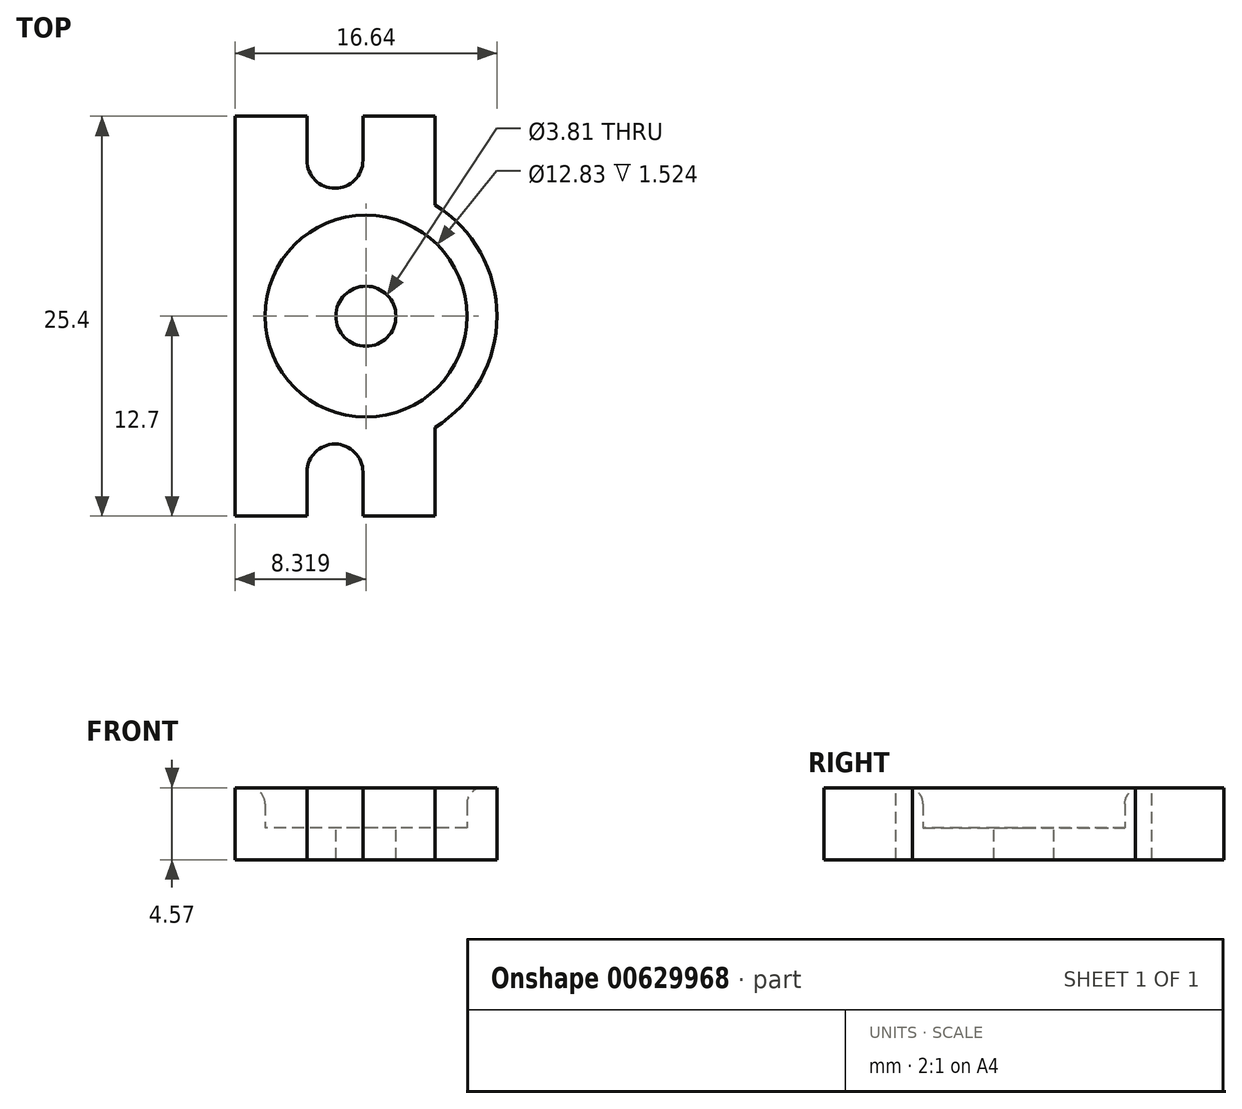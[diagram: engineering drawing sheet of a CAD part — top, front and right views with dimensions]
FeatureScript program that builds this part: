
annotation { "Feature Type Name" : "Feature", "Feature Type Description" : "" }
export const myFeature = defineFeature(function(context is Context, id is Id, definition is map)
    precondition{}
    {
        {
            var Q0;
            Q0=qCreatedBy(makeId("Top.planeOp"),FACE);
            var sketch = newSketch(context, id + "F0", { "sketchPlane" : qUnion([Q0])});
            skLineSegment(sketch, "E0.bottom", {"start": v(6.35, 12.7) * mm, "end": v(-6.35, 12.7) * mm});
            skLineSegment(sketch, "E0.top", {"start": v(6.35, -12.7) * mm, "end": v(-6.35, -12.7) * mm});
            skLineSegment(sketch, "E0.left", {"start": v(6.35, 12.7) * mm, "end": v(6.35, -12.7) * mm});
            skLineSegment(sketch, "E0.right", {"start": v(-6.35, 12.7) * mm, "end": v(-6.35, -12.7) * mm});
            skPoint(sketch, "E0.middle", {"position": v(0, 0) * mm});
            skCircle(sketch, "E1", {"center": v(0, 9.9) * mm, "radius": 1.78 * mm});
            skCircle(sketch, "E2.MirrorC", {"center": v(0, -9.9) * mm, "radius": 1.78 * mm});
            skCircle(sketch, "E3", {"center": v(1.97, 0) * mm, "radius": 8.32 * mm});
            skLineSegment(sketch, "E4", {"start": v(-1.78, 9.9) * mm, "end": v(-1.78, 12.7) * mm});
            skLineSegment(sketch, "E5.MirrorCS", {"start": v(1.78, 9.9) * mm, "end": v(1.78, 12.7) * mm});
            skLineSegment(sketch, "E6.MirrorCS", {"start": v(-1.78, -9.9) * mm, "end": v(-1.78, -12.7) * mm});
            skLineSegment(sketch, "E7.MirrorCS", {"start": v(1.78, -9.9) * mm, "end": v(1.78, -12.7) * mm});
            skCircle(sketch, "E8", {"center": v(1.97, 0) * mm, "radius": 1.9 * mm});
            skCircle(sketch, "E9", {"center": v(1.97, 0) * mm, "radius": 6.41 * mm});
            skSolve(sketch);
        }
        {
            var Q0;
            {var subQ1=sQuery(id+"F0.wireOp",EDGE,"E0.left");var subQ4=sQuery(id+"F0.wireOp",EDGE,"E3");var subQ7=makeQuery(id+"F0.imprint","INTERSECT",VERTEX,{"disambiguationData":[OD(0.0)],"derivedFrom":[subQ1,subQ4]});Q0=makeQuery(id+"F0.imprint","IMPRINT",FACE,{"disambiguationData":[TD([[makeQuery(id+"F0.imprint","IMPRINT",EDGE,{"disambiguationData":[TD([[subQ7,-1.0]])],"derivedFrom":subQ1}),-1.0]])]});}
            var Q1;
            {var subQ0=sQuery(id+"F0.wireOp",EDGE,"Um5dh8zR-fQAL-UgyF-3JbJ-gLPxUa5TkWMC");var subQ1=sQuery(id+"F0.wireOp",EDGE,"E0.left");var subQ2=makeQuery(id+"F0.imprint","INTERSECT",VERTEX,{"disambiguationData":[OD(0.0)],"derivedFrom":[subQ1,subQ0]});Q1=makeQuery(id+"F0.imprint","IMPRINT",FACE,{"disambiguationData":[TD([[makeQuery(id+"F0.imprint","IMPRINT",EDGE,{"disambiguationData":[TD([[subQ2,-1.0]])],"derivedFrom":subQ1}),-1.0]])]});}
            var Q2;
            {var subQ0=sQuery(id+"F0.wireOp",EDGE,"Um5dh8zR-fQAL-UgyF-3JbJ-gLPxUa5TkWMC");var subQ1=sQuery(id+"F0.wireOp",EDGE,"E0.left");var subQ2=makeQuery(id+"F0.imprint","INTERSECT",VERTEX,{"disambiguationData":[OD(0.0)],"derivedFrom":[subQ1,subQ0]});Q2=makeQuery(id+"F0.imprint","IMPRINT",FACE,{"disambiguationData":[TD([[makeQuery(id+"F0.imprint","IMPRINT",EDGE,{"disambiguationData":[TD([[subQ2,-1.0]])],"derivedFrom":subQ1}),1.0]])]});}
            var Q3;
            {var subQ0=sQuery(id+"F0.wireOp",EDGE,"E3");var subQ1=sQuery(id+"F0.wireOp",EDGE,"E0.left");var subQ2=makeQuery(id+"F0.imprint","INTERSECT",VERTEX,{"disambiguationData":[OD(0.0)],"derivedFrom":[subQ1,subQ0]});Q3=makeQuery(id+"F0.imprint","IMPRINT",FACE,{"disambiguationData":[TD([[makeQuery(id+"F0.imprint","IMPRINT",EDGE,{"disambiguationData":[TD([[subQ2,-1.0]])],"derivedFrom":subQ1}),1.0]])]});}
            var Q4;
            {var subQ0=sQuery(id+"F0.wireOp",EDGE,"E4");Q4=makeQuery(id+"F0.imprint","IMPRINT",FACE,{"disambiguationData":[TD([[makeQuery(id+"F0.imprint","IMPRINT",EDGE,{"derivedFrom":subQ0}),1.0]])]});}
            var Q5;
            {var subQ0=sQuery(id+"F0.wireOp",EDGE,"E5.MirrorCS");Q5=makeQuery(id+"F0.imprint","IMPRINT",FACE,{"disambiguationData":[TD([[makeQuery(id+"F0.imprint","IMPRINT",EDGE,{"derivedFrom":subQ0}),-1.0]])]});}
            var Q6;
            {var subQ5=sQuery(id+"F0.wireOp",EDGE,"E7.MirrorCS");Q6=makeQuery(id+"F0.imprint","IMPRINT",FACE,{"disambiguationData":[TD([[makeQuery(id+"F0.imprint","IMPRINT",EDGE,{"derivedFrom":subQ5}),1.0]])]});}
            var Q7;
            {var subQ7=sQuery(id+"F0.wireOp",EDGE,"E6.MirrorCS");Q7=makeQuery(id+"F0.imprint","IMPRINT",FACE,{"disambiguationData":[TD([[makeQuery(id+"F0.imprint","IMPRINT",EDGE,{"derivedFrom":subQ7}),-1.0]])]});}
            var Q8;
            Q8=makeQuery(id+"F0.imprint","IMPRINT",FACE,{"disambiguationData":[TD([[makeQuery(id+"F0.imprint","IMPRINT",EDGE,{"derivedFrom":sQuery(id+"F0.wireOp",EDGE,"E8")}),-1.0]])]});
            var Q9;
            {var subQ0=sQuery(id+"F0.wireOp",EDGE,"E9");var subQ1=sQuery(id+"F0.wireOp",EDGE,"E0.left");var subQ2=makeQuery(id+"F0.imprint","INTERSECT",VERTEX,{"disambiguationData":[OD(0.0)],"derivedFrom":[subQ1,subQ0]});Q9=makeQuery(id+"F0.imprint","IMPRINT",FACE,{"disambiguationData":[TD([[makeQuery(id+"F0.imprint","IMPRINT",EDGE,{"disambiguationData":[TD([[subQ2,-1.0]])],"derivedFrom":subQ1}),1.0]])]});}
            extrude(context, id + "F1", {"entities" : qUnion([Q0, Q1, Q2, Q3, Q4, Q5, Q6, Q7, Q8, Q9]), "oppositeDirection" : true, "depth" : 2.03 * mm, "offsetDistance" : 25.4 * mm});
        }
        {
            var Q0;
            {var subQ1=sQuery(id+"F0.wireOp",EDGE,"E0.left");var subQ4=sQuery(id+"F0.wireOp",EDGE,"E3");var subQ7=makeQuery(id+"F0.imprint","INTERSECT",VERTEX,{"disambiguationData":[OD(0.0)],"derivedFrom":[subQ1,subQ4]});Q0=makeQuery(id+"F0.imprint","IMPRINT",FACE,{"disambiguationData":[TD([[makeQuery(id+"F0.imprint","IMPRINT",EDGE,{"disambiguationData":[TD([[subQ7,-1.0]])],"derivedFrom":subQ1}),-1.0]])]});}
            var Q1;
            {var subQ0=sQuery(id+"F0.wireOp",EDGE,"E3");var subQ1=sQuery(id+"F0.wireOp",EDGE,"E0.left");var subQ2=makeQuery(id+"F0.imprint","INTERSECT",VERTEX,{"disambiguationData":[OD(0.0)],"derivedFrom":[subQ1,subQ0]});Q1=makeQuery(id+"F0.imprint","IMPRINT",FACE,{"disambiguationData":[TD([[makeQuery(id+"F0.imprint","IMPRINT",EDGE,{"disambiguationData":[TD([[subQ2,-1.0]])],"derivedFrom":subQ1}),1.0]])]});}
            var Q2;
            {var subQ0=sQuery(id+"F0.wireOp",EDGE,"E5.MirrorCS");Q2=makeQuery(id+"F0.imprint","IMPRINT",FACE,{"disambiguationData":[TD([[makeQuery(id+"F0.imprint","IMPRINT",EDGE,{"derivedFrom":subQ0}),-1.0]])]});}
            var Q3;
            {var subQ0=sQuery(id+"F0.wireOp",EDGE,"E4");Q3=makeQuery(id+"F0.imprint","IMPRINT",FACE,{"disambiguationData":[TD([[makeQuery(id+"F0.imprint","IMPRINT",EDGE,{"derivedFrom":subQ0}),1.0]])]});}
            var Q4;
            {var subQ5=sQuery(id+"F0.wireOp",EDGE,"E7.MirrorCS");Q4=makeQuery(id+"F0.imprint","IMPRINT",FACE,{"disambiguationData":[TD([[makeQuery(id+"F0.imprint","IMPRINT",EDGE,{"derivedFrom":subQ5}),1.0]])]});}
            var Q5;
            {var subQ7=sQuery(id+"F0.wireOp",EDGE,"E6.MirrorCS");Q5=makeQuery(id+"F0.imprint","IMPRINT",FACE,{"disambiguationData":[TD([[makeQuery(id+"F0.imprint","IMPRINT",EDGE,{"derivedFrom":subQ7}),-1.0]])]});}
            extrude(context, id + "F2", {"entities" : qUnion([Q0, Q1, Q2, Q3, Q4, Q5]), "operationType" : NewBodyOperationType.ADD, "depth" : 2.54 * mm, "offsetDistance" : 25.4 * mm});
        }
        {
            var Q0;
            Q0=makeQuery(id+"F2.opExtrude","CAP_EDGE",EDGE,{"disambiguationData":[OSD([sQuery(id+"F0.wireOp",EDGE,"E9")])],"isStart":false});
            fillet(context, id + "F3", {"entities" : qUnion([Q0]), "radius" : 1.02 * mm, "tangentPropagation" : true, "allowEdgeOverflow" : false});
        }
    });
